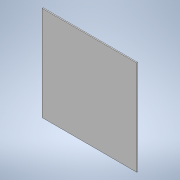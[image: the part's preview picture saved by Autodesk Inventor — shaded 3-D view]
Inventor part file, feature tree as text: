
AUTODESK INVENTOR PART (.ipt)
format: ipt  version: 2022 (Build 260153000, 153)  size: 93,696 bytes
history: native  units: mm
features: sheet_metal_op x1, sketch x1, other x1
ambient origin geometry x8: Origin, YZ Plane, XZ Plane, XY Plane, X Axis, Y Axis, Z Axis, Center Point
bodies: Solid1 (feature_tree)
feature tree (3):
  sheet_metal_op  "Face1"
  sketch  "Sketch1"  dims[d0=300.0mm d1=300.0mm d2=3.175mm]
  other  "Plate1"
